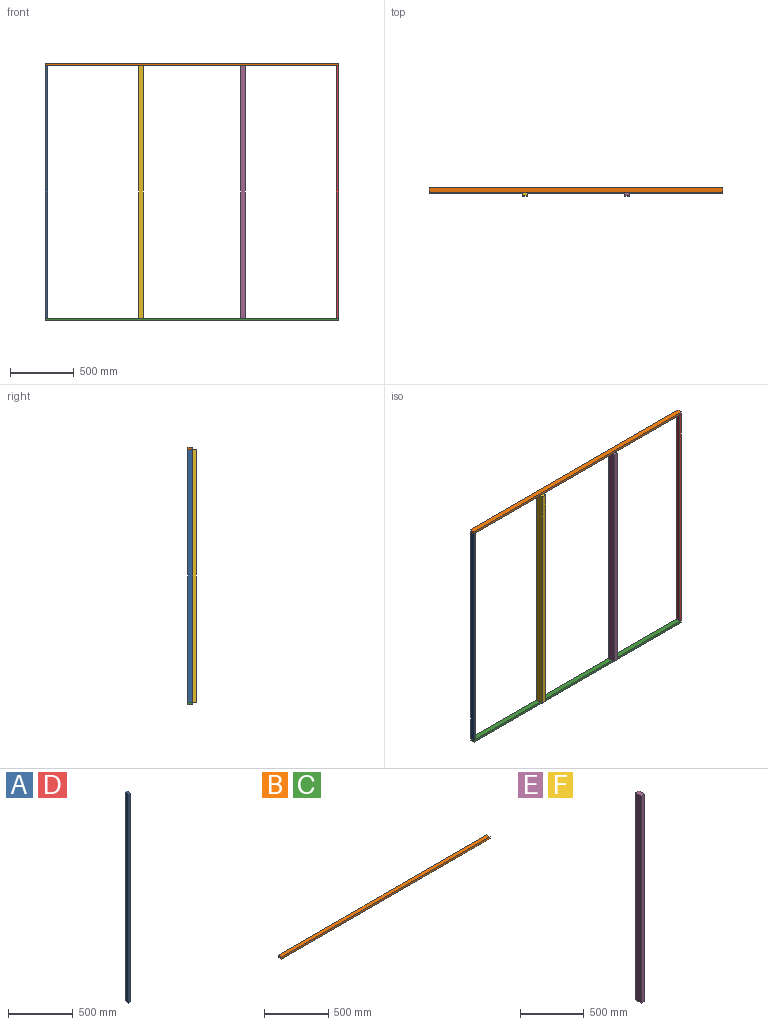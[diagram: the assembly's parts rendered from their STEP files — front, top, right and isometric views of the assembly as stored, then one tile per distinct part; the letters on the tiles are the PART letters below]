
ASSEMBLY  parts=6 mates=5
PART A: 6 faces, bbox 19.1x38.1x1981.2 mm
  f0: plane 38.1x19.05mm, normal (0,0,1), area 725.8mm2, adj f1,f3,f4,f5
  f1: plane 1981.2x19.05mm, normal (0,1,0), area 37741.9mm2, adj f0,f2,f3,f4
  f2: plane 38.1x19.05mm, normal (0,0,-1), area 725.8mm2, adj f1,f3,f4,f5
  f3: plane 1981.2x38.1mm, normal (-1,0,0), area 75483.7mm2, adj f0,f1,f2,f5
  f4: plane 1981.2x38.1mm, normal (1,0,0), area 75483.7mm2, adj f0,f1,f2,f5
  f5: plane 1981.2x19.05mm, normal (0,-1,0), area 37741.9mm2, adj f0,f2,f3,f4
PART B: 6 faces, bbox 2298.7x38.1x19.1 mm
  f0: plane 38.1x19.05mm, normal (1,0,0), area 725.8mm2, adj f1,f2,f3,f4
  f1: plane 2298.7x19.05mm, normal (0,-1,0), area 43790.2mm2, adj f0,f2,f4,f5
  f2: plane 2298.7x38.1mm, normal (0,0,-1), area 87580.5mm2, adj f0,f1,f3,f5
  f3: plane 2298.7x19.05mm, normal (0,1,0), area 43790.2mm2, adj f0,f2,f4,f5
  f4: plane 2298.7x38.1mm, normal (0,0,1), area 87580.5mm2, adj f0,f1,f3,f5
  f5: plane 38.1x19.05mm, normal (-1,0,0), area 725.8mm2, adj f1,f2,f3,f4
PART C: same geometry as B
PART D: same geometry as A
PART E: 6 faces, bbox 38.1x63.5x1981.2 mm
  f0: plane 1981.2x63.5mm, normal (-1,0,0), area 125806.2mm2, adj f1,f3,f4,f5
  f1: plane 1981.2x38.1mm, normal (0,-1,0), area 75483.7mm2, adj f0,f2,f4,f5
  f2: plane 1981.2x63.5mm, normal (1,0,0), area 125806.2mm2, adj f1,f3,f4,f5
  f3: plane 1981.2x38.1mm, normal (0,1,0), area 75483.7mm2, adj f0,f2,f4,f5
  f4: plane 63.5x38.1mm, normal (0,0,1), area 2419.4mm2, adj f0,f1,f2,f3
  f5: plane 63.5x38.1mm, normal (0,0,-1), area 2419.4mm2, adj f0,f1,f2,f3
PART F: same geometry as E
PLACE A t=(311.3,288.02,162.44)mm
PLACE B t=(311.3,288.02,2162.69)mm
PLACE C t=(311.3,288.02,162.44)mm
PLACE D t=(2590.95,288.02,162.44)mm
PLACE E t=(863.75,288.02,162.44)mm
PLACE F t=(63.65,288.02,162.44)mm
MATE fastened E.f5 <-> C.f4  axis (0,0,-1) through (1911.5,192.77,220.86)mm
MATE fastened A.f2 <-> C.f4  axis (0,0,-1) through (381.15,218.17,220.86)mm
MATE fastened D.f2 <-> C.f4  axis (0,0,-1) through (2679.85,218.17,220.86)mm
MATE fastened D.f0 <-> B.f2  axis (0,0,1) through (2679.85,218.17,2202.06)mm
MATE fastened F.f5 <-> C.f4  axis (0,0,-1) through (1149.5,192.77,220.86)mm
